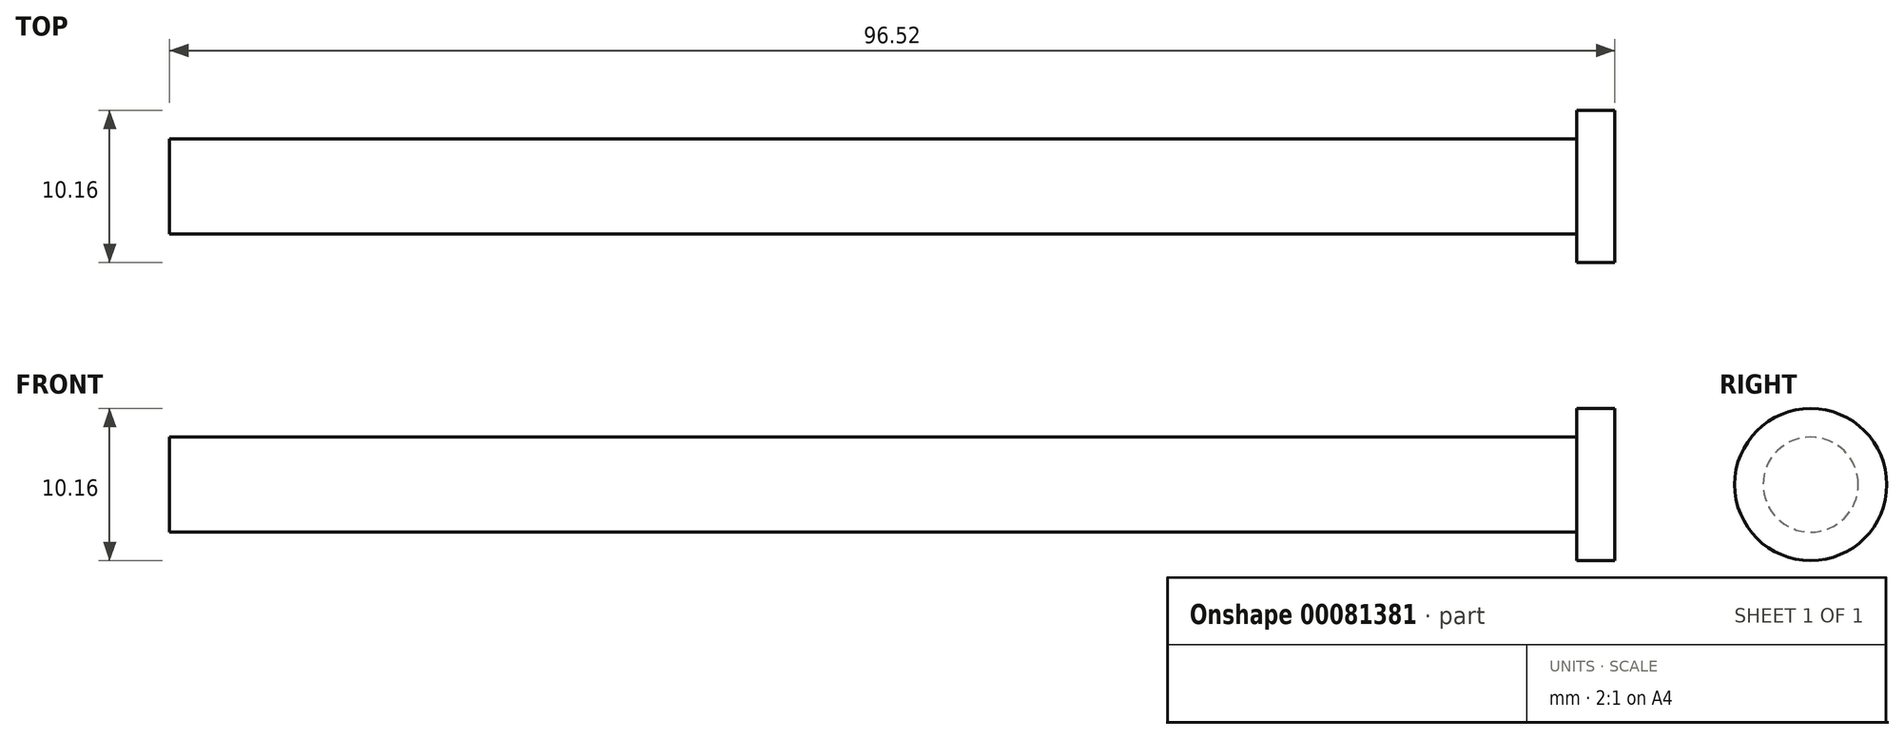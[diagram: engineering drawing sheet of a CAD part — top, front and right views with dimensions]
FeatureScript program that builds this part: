
annotation { "Feature Type Name" : "Feature", "Feature Type Description" : "" }
export const myFeature = defineFeature(function(context is Context, id is Id, definition is map)
    precondition{}
    {
        {
            var Q0;
            Q0=qCreatedBy(makeId("Right.planeOp"),FACE);
            var sketch = newSketch(context, id + "F0", { "sketchPlane" : qUnion([Q0])});
            skCircle(sketch, "E0", {"center": v(0, 0) * mm, "radius": 3.18 * mm});
            skSolve(sketch);
        }
        {
            var Q0;
            Q0 = qSketchRegion(id + "F0", true);
            extrude(context, id + "F1", {"entities" : qUnion([Q0]), "endBound" : BoundingType.SYMMETRIC, "depth" : 96.52 * mm});
        }
        {
            var Q0;
            Q0=makeQuery(id+"F1.opExtrude","CAP_FACE",FACE,{"disambiguationData":[OSD([sQuery(id+"F0.wireOp",EDGE,"E0")])],"isStart":false});
            var sketch = newSketch(context, id + "F2", { "sketchPlane" : qUnion([Q0])});
            skCircle(sketch, "E1", {"center": v(0, 0) * mm, "radius": 5.08 * mm});
            skSolve(sketch);
        }
        {
            var Q0;
            Q0 = qSketchRegion(id + "F2", true);
            extrude(context, id + "F3", {"entities" : qUnion([Q0]), "operationType" : NewBodyOperationType.ADD, "oppositeDirection" : true, "depth" : 2.54 * mm});
        }
    });
